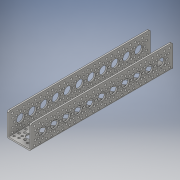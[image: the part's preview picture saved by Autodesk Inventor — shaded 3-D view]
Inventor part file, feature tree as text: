
AUTODESK INVENTOR PART (.ipt)
format: ipt  version: 2016 (Build 200138000, 138)  size: 783,872 bytes
history: native  units: in
note: dims shown in document units (in); Inventor stores cm internally (conversion verified against a paired STEP export)
features: direct_edit x1, fillet x1, move_body x1
ambient origin geometry x8: Origin, YZ Plane, XZ Plane, XY Plane, X Axis, Y Axis, Z Axis, Center Point
bodies: Solid1 (feature_tree)
feature tree (3):
  direct_edit  "Direct Edit1"
  fillet  "Fillet1"  Radius=0.02in
  move_body  "Move1"
